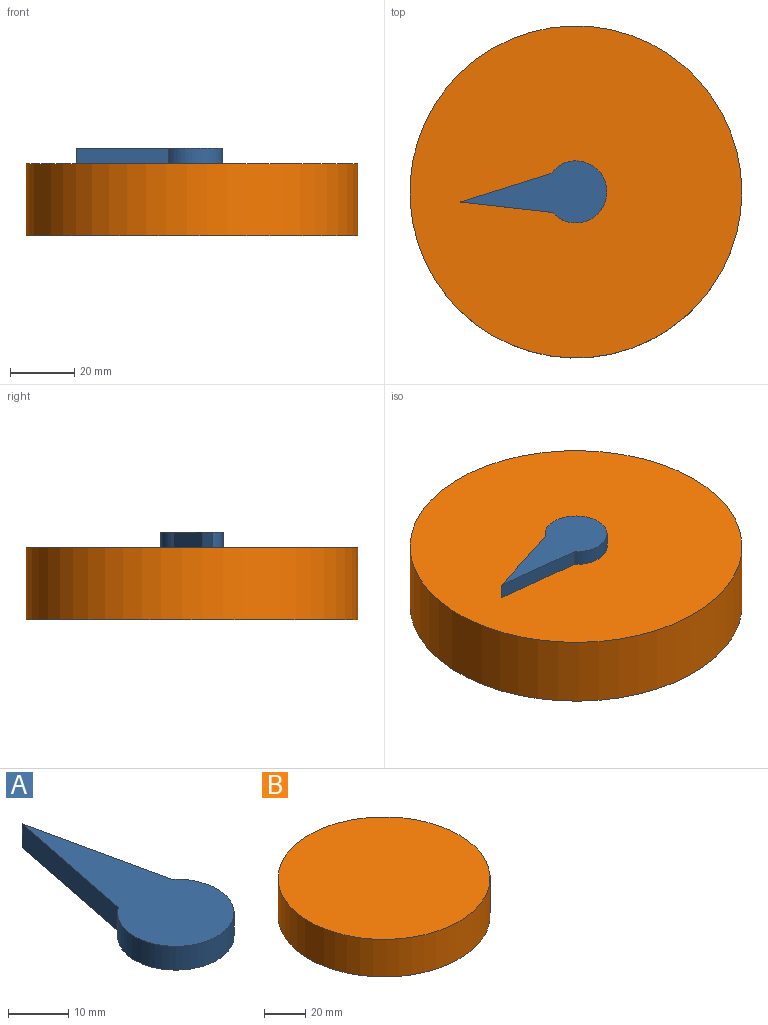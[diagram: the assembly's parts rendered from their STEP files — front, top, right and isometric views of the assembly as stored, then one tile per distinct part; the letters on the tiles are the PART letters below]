
ASSEMBLY  parts=2 mates=1
PART A: 5 faces, bbox 19.3x45.7x4.8 mm
  f0: cylinder r=9.64mm len=19.27mm, axis (0,0,-1), area 229.2mm2, adj f1,f2,f3,f4
  f1: plane 28.76x6.34mm, normal (0.98,0.22,0), area 142.1mm2, adj f0,f2,f3,f4
  f2: plane 28.27x5.72mm, normal (-0.98,0.2,0), area 139.2mm2, adj f0,f1,f3,f4
  f3: plane 45.65x19.27mm, normal (0,0,1), area 446.1mm2, adj f0,f1,f2
  f4: plane 45.65x19.27mm, normal (0,0,-1), area 446.1mm2, adj f0,f1,f2
PART B: 3 faces, bbox 103.1x103.1x22.4 mm
  f0: cylinder r=51.55mm len=103.1mm, axis (0,0,-1), area 7239.5mm2, adj f1,f2
  f1: plane 103.1x103.1mm, normal (0,0,1), area 8347.8mm2, adj f0
  f2: plane 103.1x103.1mm, normal (0,0,-1), area 8347.8mm2, adj f0
PLACE A rot(axis=(0,0,1),95deg) t=(0,0,0)mm
PLACE B at identity fixed
MATE revolute B.f0 <-> A.f0  axis (0,0,1) through (0,0,22.35)mm
